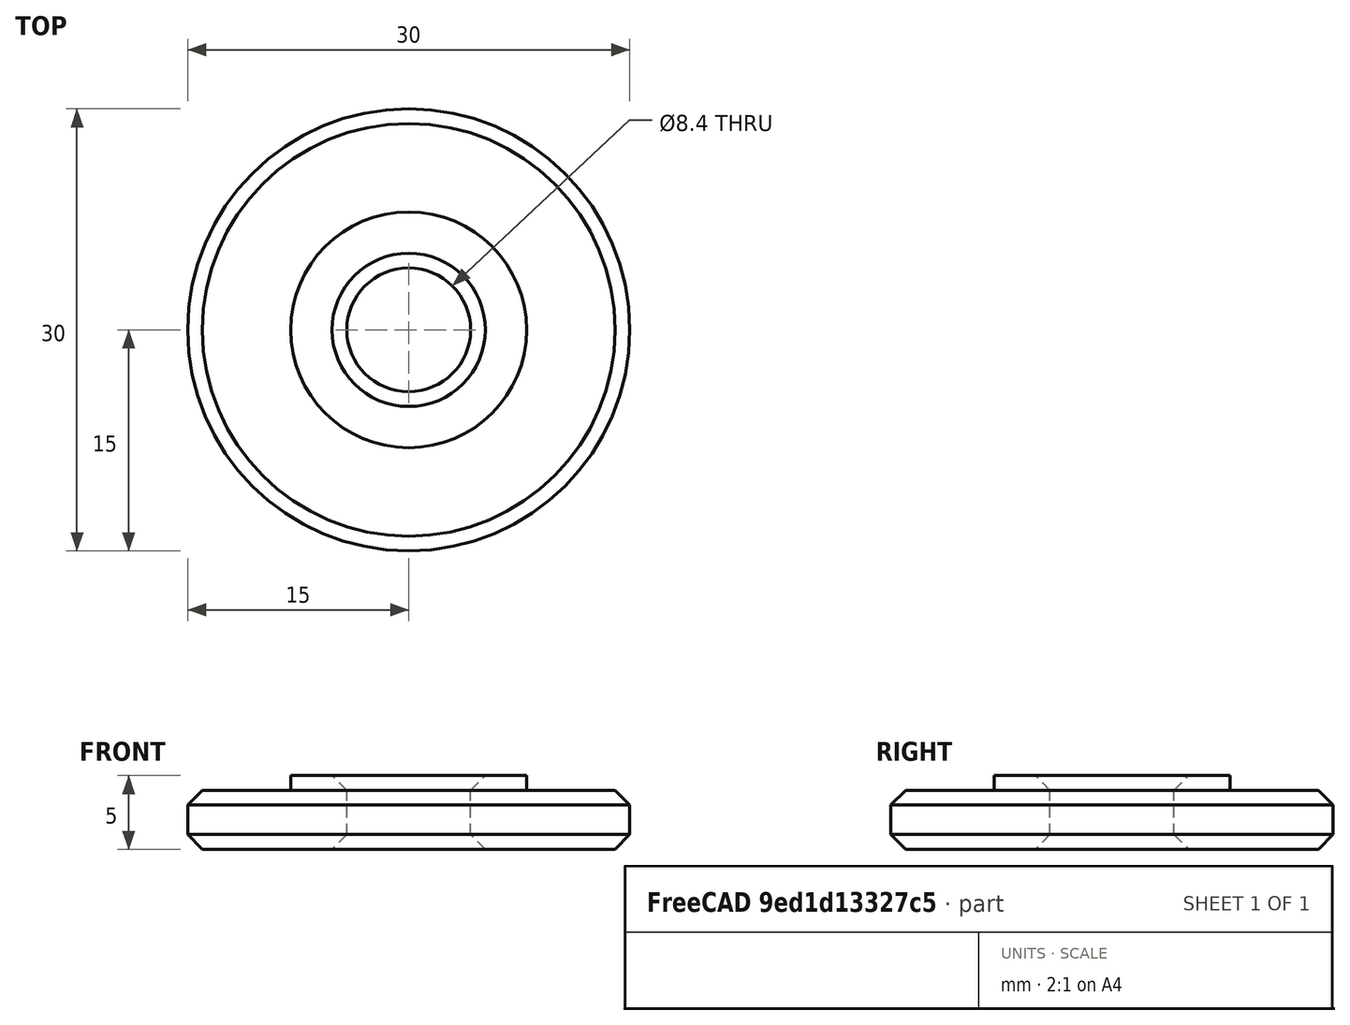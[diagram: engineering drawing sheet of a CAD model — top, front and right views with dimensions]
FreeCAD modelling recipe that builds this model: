
FCSTD DOCUMENT  (FreeCAD 0.18.4R)
Label: lawnmower-spacer
License: All rights reserved
LicenseURL: http://en.wikipedia.org/wiki/All_rights_reserved
objects: PartDesign::AdditiveCylinder×2, PartDesign::Chamfer×2, PartDesign::SubtractiveCylinder×1, PartDesign::Body×1
note: 9 computed .brp shape members not serialized (recipe doc carries the construction recipe); baked Part::Feature solids carry a one-line shape summary decoded from their .brp

FEATURE [PartDesign::AdditiveCylinder] Cylinder
  Angle = 360
  AttacherType = Attacher::AttachEngine3D
  Height = 4
  Radius = 15
  Refine = true
FEATURE [PartDesign::AdditiveCylinder] Cylinder002
  Angle = 360
  AttacherType = Attacher::AttachEngine3D
  BaseFeature = -> Cylinder
  Height = 5
  Radius = 8
  Refine = true
FEATURE [PartDesign::SubtractiveCylinder] Cylinder003
  Angle = 360
  AttacherType = Attacher::AttachEngine3D
  BaseFeature = -> Cylinder002
  Height = 10
  Radius = 4.2
  Refine = true
FEATURE [PartDesign::Chamfer] Chamfer
  Base = -> Cylinder003 [Face1]
  BaseFeature = -> Cylinder003
  Size = 1
FEATURE [PartDesign::Chamfer] Chamfer001
  Base = -> Chamfer [Face6]
  BaseFeature = -> Chamfer
  Size = 1
FEATURE [PartDesign::Body] Body001
  Group = -> [Cylinder,Cylinder002,Cylinder003,Chamfer,Chamfer001]
  Origin = -> Origin001
  Tip = -> Chamfer001
